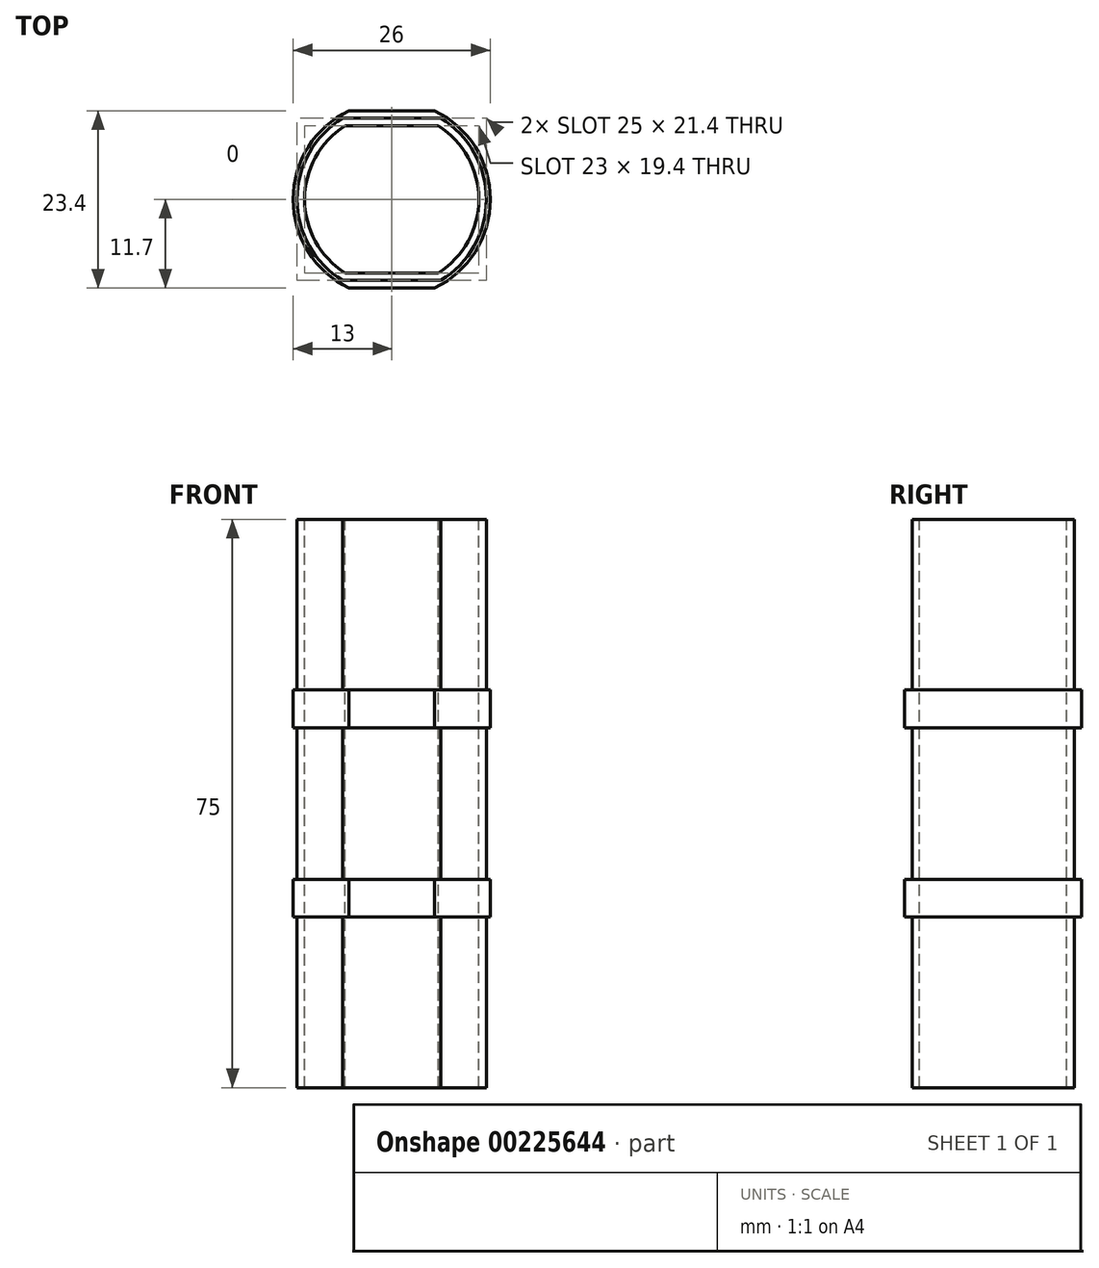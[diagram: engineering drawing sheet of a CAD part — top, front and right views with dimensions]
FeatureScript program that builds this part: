
annotation { "Feature Type Name" : "Feature", "Feature Type Description" : "" }
export const myFeature = defineFeature(function(context is Context, id is Id, definition is map)
    precondition{}
    {
        {
            var Q0;
            Q0=qCreatedBy(makeId("Top.planeOp"),FACE);
            var sketch = newSketch(context, id + "F0", { "sketchPlane" : qUnion([Q0])});
            skCircle(sketch, "E0", {"center": v(0, 0) * mm, "radius": 6.5 * mm});
            skCircle(sketch, "E1", {"center": v(0, 0) * mm, "radius": 11.5 * mm});
            skSolve(sketch);
        }
        {
            var Q0;
            Q0 = qSketchRegion(id + "F0", true);
            extrude(context, id + "F1", {"entities" : qUnion([Q0]), "depth" : 75 * mm});
        }
        {
            var Q0;
            Q0=makeQuery(id+"F1.opExtrude","CAP_FACE",FACE,{"disambiguationData":[OSD([sQuery(id+"F0.wireOp",EDGE,"E0"),sQuery(id+"F0.wireOp",EDGE,"E1")])],"isStart":false});
            var sketch = newSketch(context, id + "F2", { "sketchPlane" : qUnion([Q0])});
            skLineSegment(sketch, "E2.bottom", {"start": v(20, -9.7) * mm, "end": v(-20, -9.7) * mm});
            skLineSegment(sketch, "E2.top", {"start": v(20, 9.7) * mm, "end": v(-20, 9.7) * mm});
            skPoint(sketch, "E2.middle", {"position": v(0, 0) * mm});
            skLineSegment(sketch, "E3", {"start": v(-20, -9.7) * mm, "end": v(-20, -32.48) * mm});
            skLineSegment(sketch, "E4", {"start": v(-20, -32.48) * mm, "end": v(20, -32.48) * mm});
            skLineSegment(sketch, "E5", {"start": v(20, -32.48) * mm, "end": v(20, -9.7) * mm});
            skLineSegment(sketch, "E6", {"start": v(-20, 9.7) * mm, "end": v(-20, 28.79) * mm});
            skLineSegment(sketch, "E7", {"start": v(-20, 28.79) * mm, "end": v(20, 33.53) * mm});
            skLineSegment(sketch, "E8", {"start": v(20, 33.53) * mm, "end": v(20, 9.7) * mm});
            skSolve(sketch);
        }
        {
            var Q0;
            Q0 = qSketchRegion(id + "F2", true);
            var Q1;
            Q1=makeQuery(id+"F1.opExtrude","CAP_FACE",FACE,{"disambiguationData":[OSD([sQuery(id+"F0.wireOp",EDGE,"E0"),sQuery(id+"F0.wireOp",EDGE,"E1")])],"isStart":true});
            extrude(context, id + "F3", {"entities" : qUnion([Q0]), "operationType" : NewBodyOperationType.REMOVE, "endBound" : BoundingType.UP_TO_SURFACE, "oppositeDirection" : true, "endBoundEntityFace" : qUnion([Q1]), "depth" : 25 * mm});
        }
        {
            var Q0;
            Q0=makeQuery(id+"F1.opExtrude","CAP_FACE",FACE,{"disambiguationData":[OSD([sQuery(id+"F0.wireOp",EDGE,"E0"),sQuery(id+"F0.wireOp",EDGE,"E1")])],"isStart":false});
            var sketch = newSketch(context, id + "F4", { "sketchPlane" : qUnion([Q0])});
            skArc(sketch, "E9", {"start": v(-6.46, 10.7) * mm, "mid": v(-12.5, 0) * mm, "end": v(-6.46, -10.7) * mm});
            skArc(sketch, "E10", {"start": v(-6.18, 9.7) * mm, "mid": v(-11.5, 0) * mm, "end": v(-6.18, -9.7) * mm});
            skLineSegment(sketch, "E11", {"start": v(-6.18, 9.7) * mm, "end": v(6.18, 9.7) * mm});
            skLineSegment(sketch, "E12", {"start": v(6.18, -9.7) * mm, "end": v(-6.18, -9.7) * mm});
            skArc(sketch, "E13.trimOffspring", {"start": v(6.18, -9.7) * mm, "mid": v(11.5, 0) * mm, "end": v(6.18, 9.7) * mm});
            skLineSegment(sketch, "E14", {"start": v(-6.46, 10.7) * mm, "end": v(6.46, 10.7) * mm});
            skLineSegment(sketch, "E15", {"start": v(-6.46, -10.7) * mm, "end": v(6.46, -10.7) * mm});
            skArc(sketch, "E16.trimOffspring", {"start": v(6.46, -10.7) * mm, "mid": v(12.5, 0) * mm, "end": v(6.46, 10.7) * mm});
            skSolve(sketch);
        }
        {
            var Q0;
            Q0 = qSketchRegion(id + "F4", true);
            extrude(context, id + "F5", {"entities" : qUnion([Q0]), "operationType" : NewBodyOperationType.ADD, "oppositeDirection" : true, "depth" : 75 * mm});
        }
        {
            var Q0;
            Q0=makeQuery(id+"F5.boolean.opBoolean","MERGE",FACE,{"derivedFrom":[makeQuery(id+"F1.opExtrude","CAP_FACE",FACE,{"disambiguationData":[OSD([sQuery(id+"F0.wireOp",EDGE,"E0"),sQuery(id+"F0.wireOp",EDGE,"E1")])],"isStart":false}),makeQuery(id+"F5.opExtrude","CAP_FACE",FACE,{"disambiguationData":[OSD([sQuery(id+"F4.wireOp",EDGE,"E9"),sQuery(id+"F4.wireOp",EDGE,"E10"),sQuery(id+"F4.wireOp",EDGE,"E11"),sQuery(id+"F4.wireOp",EDGE,"E12"),sQuery(id+"F4.wireOp",EDGE,"E13.trimOffspring")])],"isStart":true})]});
            var sketch = newSketch(context, id + "F6", { "sketchPlane" : qUnion([Q0])});
            skArc(sketch, "E17", {"start": v(6.18, -9.7) * mm, "mid": v(11.5, 0) * mm, "end": v(6.18, 9.7) * mm});
            skLineSegment(sketch, "E18", {"start": v(6.18, 9.7) * mm, "end": v(-6.18, 9.7) * mm});
            skLineSegment(sketch, "E19", {"start": v(6.18, -9.7) * mm, "end": v(-6.18, -9.7) * mm});
            skArc(sketch, "E20.trimOffspring", {"start": v(-6.18, 9.7) * mm, "mid": v(-11.5, 0) * mm, "end": v(-6.18, -9.7) * mm});
            skSolve(sketch);
        }
        {
            var Q0;
            Q0 = qSketchRegion(id + "F6", true);
            extrude(context, id + "F7", {"entities" : qUnion([Q0]), "operationType" : NewBodyOperationType.REMOVE, "oppositeDirection" : true, "depth" : 75 * mm});
        }
        {
            var Q0;
            Q0=makeQuery(id+"F5.boolean.opBoolean","MERGE",FACE,{"derivedFrom":[makeQuery(id+"F1.opExtrude","CAP_FACE",FACE,{"disambiguationData":[OSD([sQuery(id+"F0.wireOp",EDGE,"E0"),sQuery(id+"F0.wireOp",EDGE,"E1")])],"isStart":false}),makeQuery(id+"F5.opExtrude","CAP_FACE",FACE,{"disambiguationData":[OSD([sQuery(id+"F4.wireOp",EDGE,"E9"),sQuery(id+"F4.wireOp",EDGE,"E10"),sQuery(id+"F4.wireOp",EDGE,"E11"),sQuery(id+"F4.wireOp",EDGE,"E12"),sQuery(id+"F4.wireOp",EDGE,"E13.trimOffspring"),sQuery(id+"F4.wireOp",EDGE,"E14"),sQuery(id+"F4.wireOp",EDGE,"E15"),sQuery(id+"F4.wireOp",EDGE,"E16.trimOffspring")])],"isStart":true})]});
            var Q1;
            Q1=makeQuery(id+"F5.boolean.opBoolean","MERGE",FACE,{"derivedFrom":[makeQuery(id+"F1.opExtrude","CAP_FACE",FACE,{"disambiguationData":[OSD([sQuery(id+"F0.wireOp",EDGE,"E0"),sQuery(id+"F0.wireOp",EDGE,"E1")])],"isStart":true}),makeQuery(id+"F5.opExtrude","CAP_FACE",FACE,{"disambiguationData":[OSD([sQuery(id+"F4.wireOp",EDGE,"E9"),sQuery(id+"F4.wireOp",EDGE,"E10"),sQuery(id+"F4.wireOp",EDGE,"E11"),sQuery(id+"F4.wireOp",EDGE,"E12"),sQuery(id+"F4.wireOp",EDGE,"E13.trimOffspring"),sQuery(id+"F4.wireOp",EDGE,"E14"),sQuery(id+"F4.wireOp",EDGE,"E15"),sQuery(id+"F4.wireOp",EDGE,"E16.trimOffspring")])],"isStart":false})]});
            cPlane(context, id + "F8", {"entities" : qUnion([Q0, Q1]), "cplaneType" : CPlaneType.MID_PLANE, "offset" : 25 * mm, "width" : 150 * mm, "height" : 150 * mm});
        }
        {
            var Q0;
            Q0=qCreatedBy(id+"F8.planeOp",FACE);
            var sketch = newSketch(context, id + "F9", { "sketchPlane" : qUnion([Q0])});
            skArc(sketch, "E21", {"start": v(-5.67, 11.7) * mm, "mid": v(-13, 0) * mm, "end": v(-5.67, -11.7) * mm});
            skLineSegment(sketch, "E22", {"start": v(5.67, -11.7) * mm, "end": v(-5.67, -11.7) * mm});
            skLineSegment(sketch, "E23", {"start": v(5.67, 11.7) * mm, "end": v(-5.67, 11.7) * mm});
            skArc(sketch, "E24.trimOffspring", {"start": v(5.67, -11.7) * mm, "mid": v(13, 0) * mm, "end": v(5.67, 11.7) * mm});
            skArc(sketch, "E25", {"start": v(-6.18, 9.7) * mm, "mid": v(-11.5, 0) * mm, "end": v(-6.18, -9.7) * mm});
            skLineSegment(sketch, "E26", {"start": v(6.18, 9.7) * mm, "end": v(-6.18, 9.7) * mm});
            skLineSegment(sketch, "E27", {"start": v(6.18, -9.7) * mm, "end": v(-6.18, -9.7) * mm});
            skArc(sketch, "E28.trimOffspring", {"start": v(6.18, -9.7) * mm, "mid": v(11.5, 0) * mm, "end": v(6.18, 9.7) * mm});
            skSolve(sketch);
        }
        {
            var Q0;
            Q0 = qSketchRegion(id + "F9", true);
            extrude(context, id + "F10", {"entities" : qUnion([Q0]), "operationType" : NewBodyOperationType.ADD, "endBound" : BoundingType.SYMMETRIC, "depth" : 30 * mm});
        }
        {
            var Q0;
            Q0=qCreatedBy(id+"F8.planeOp",FACE);
            var sketch = newSketch(context, id + "F11", { "sketchPlane" : qUnion([Q0])});
            skArc(sketch, "E29", {"start": v(5.67, -11.7) * mm, "mid": v(13, 0) * mm, "end": v(5.67, 11.7) * mm});
            skLineSegment(sketch, "E30", {"start": v(-5.67, -11.7) * mm, "end": v(5.67, -11.7) * mm});
            skLineSegment(sketch, "E31", {"start": v(-5.67, 11.7) * mm, "end": v(5.67, 11.7) * mm});
            skArc(sketch, "E32.trimOffspring", {"start": v(-5.67, 11.7) * mm, "mid": v(-13, 0) * mm, "end": v(-5.67, -11.7) * mm});
            skArc(sketch, "E33", {"start": v(6.46, -10.7) * mm, "mid": v(12.5, 0) * mm, "end": v(6.46, 10.7) * mm});
            skLineSegment(sketch, "E34", {"start": v(-6.46, -10.7) * mm, "end": v(6.46, -10.7) * mm});
            skLineSegment(sketch, "E35", {"start": v(-6.46, 10.7) * mm, "end": v(6.46, 10.7) * mm});
            skArc(sketch, "E36.trimOffspring", {"start": v(-6.46, 10.7) * mm, "mid": v(-12.5, 0) * mm, "end": v(-6.46, -10.7) * mm});
            skSolve(sketch);
        }
        {
            var Q0;
            Q0 = qSketchRegion(id + "F11", true);
            extrude(context, id + "F12", {"entities" : qUnion([Q0]), "operationType" : NewBodyOperationType.REMOVE, "endBound" : BoundingType.SYMMETRIC, "oppositeDirection" : true, "depth" : 20 * mm});
        }
    });
